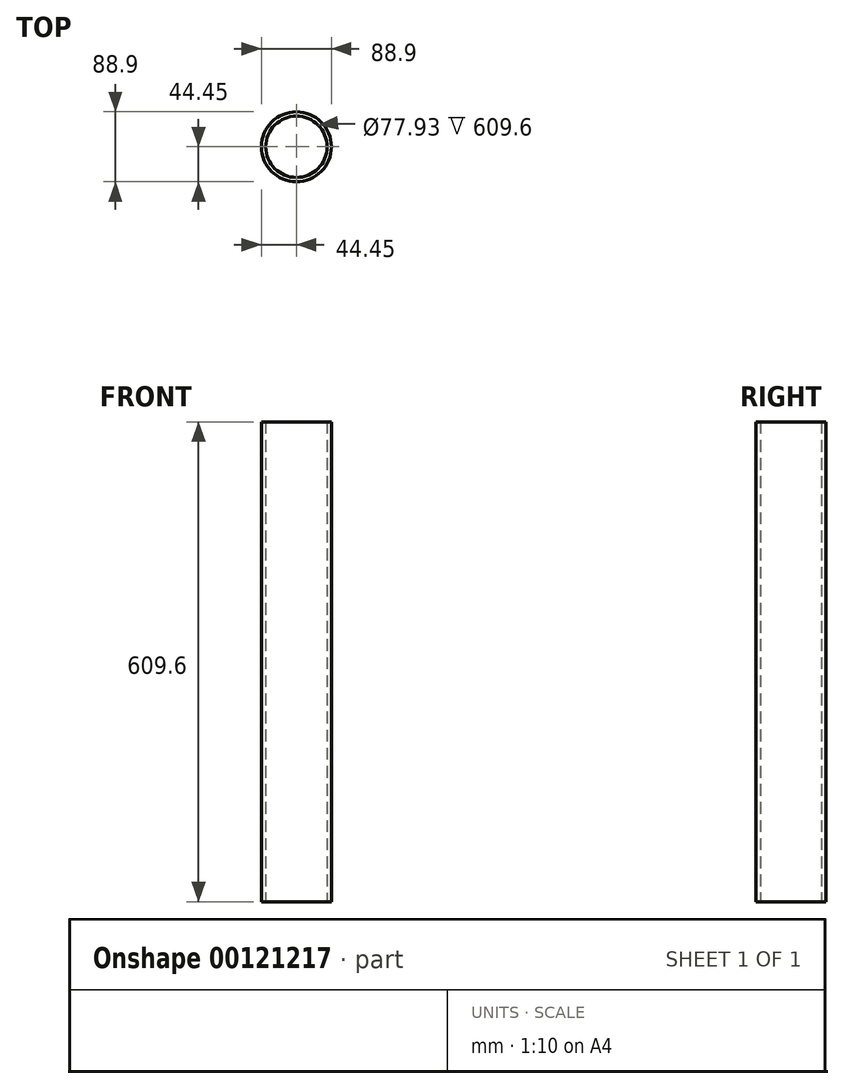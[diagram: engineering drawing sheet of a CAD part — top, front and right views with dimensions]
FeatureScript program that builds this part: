
annotation { "Feature Type Name" : "Feature", "Feature Type Description" : "" }
export const myFeature = defineFeature(function(context is Context, id is Id, definition is map)
    precondition{}
    {
        {
            var Q0;
            Q0=qCreatedBy(makeId("Top.planeOp"),FACE);
            var sketch = newSketch(context, id + "F0", { "sketchPlane" : qUnion([Q0])});
            skCircle(sketch, "E0", {"center": v(0, 0) * mm, "radius": 44.45 * mm});
            skCircle(sketch, "E1", {"center": v(0, 0) * mm, "radius": 38.96 * mm});
            skSolve(sketch);
        }
        {
            var Q0;
            Q0=qSketchRegion(id+"F0",true);
            extrude(context, id + "F1", {"entities" : qUnion([Q0]), "depth" : 609.6 * mm});
        }
    });
